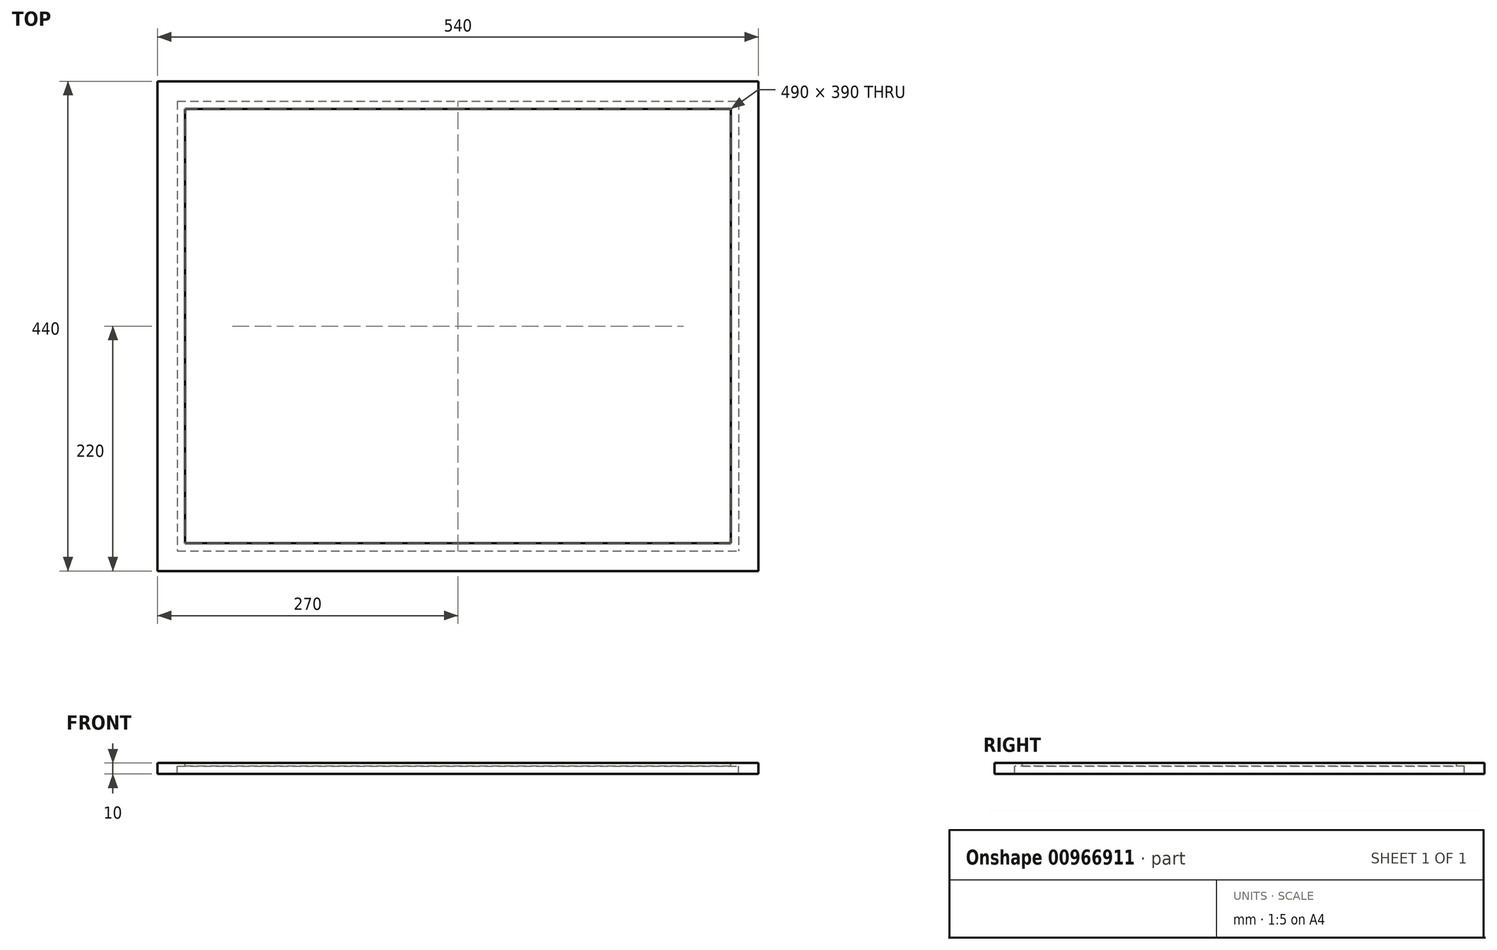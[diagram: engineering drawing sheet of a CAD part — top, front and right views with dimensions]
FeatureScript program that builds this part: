
annotation { "Feature Type Name" : "Feature", "Feature Type Description" : "" }
export const myFeature = defineFeature(function(context is Context, id is Id, definition is map)
    precondition{}
    {
        {
            var Q0;
            Q0=qCreatedBy(makeId("Top.planeOp"),FACE);
            var sketch = newSketch(context, id + "F0", { "sketchPlane" : qUnion([Q0])});
            skLineSegment(sketch, "E0.bottom", {"start": v(-270, 220) * mm, "end": v(270, 220) * mm});
            skLineSegment(sketch, "E0.top", {"start": v(-270, -220) * mm, "end": v(270, -220) * mm});
            skLineSegment(sketch, "E0.left", {"start": v(-270, 220) * mm, "end": v(-270, -220) * mm});
            skLineSegment(sketch, "E0.right", {"start": v(270, 220) * mm, "end": v(270, -220) * mm});
            skLineSegment(sketch, "E1.bottom", {"start": v(245, -195) * mm, "end": v(-245, -195) * mm});
            skLineSegment(sketch, "E1.top", {"start": v(245, 195) * mm, "end": v(-245, 195) * mm});
            skLineSegment(sketch, "E1.left", {"start": v(245, -195) * mm, "end": v(245, 195) * mm});
            skLineSegment(sketch, "E1.right", {"start": v(-245, -195) * mm, "end": v(-245, 195) * mm});
            skArc(sketch, "E2", {"start": v(270, 195) * mm, "mid": v(262.68, 212.68) * mm, "end": v(245, 220) * mm, "construction": true});
            skLineSegment(sketch, "E3.bottom", {"start": v(-252, 202) * mm, "end": v(252, 202) * mm});
            skLineSegment(sketch, "E3.top", {"start": v(-252, -202) * mm, "end": v(252, -202) * mm});
            skLineSegment(sketch, "E3.left", {"start": v(-252, 202) * mm, "end": v(-252, -202) * mm});
            skLineSegment(sketch, "E3.right", {"start": v(252, 202) * mm, "end": v(252, -202) * mm});
            skArc(sketch, "E4.trimOffspring", {"start": v(252, 195) * mm, "mid": v(249.95, 199.95) * mm, "end": v(245, 202) * mm, "construction": true});
            skSolve(sketch);
        }
        {
            var Q0;
            Q0=makeQuery(id+"F0.imprint","IMPRINT",FACE,{"disambiguationData":[TD([[makeQuery(id+"F0.imprint","IMPRINT",EDGE,{"derivedFrom":sQuery(id+"F0.wireOp",EDGE,"E0.bottom")}),-1.0]])]});
            var Q1;
            Q1=makeQuery(id+"F0.imprint","IMPRINT",FACE,{"disambiguationData":[TD([[makeQuery(id+"F0.imprint","IMPRINT",EDGE,{"derivedFrom":sQuery(id+"F0.wireOp",EDGE,"E1.bottom")}),1.0]])]});
            extrude(context, id + "F1", {"entities" : qUnion([Q0, Q1]), "oppositeDirection" : true, "depth" : 3 * mm, "offsetDistance" : 25 * mm});
        }
        {
            var Q0;
            Q0=makeQuery(id+"F0.imprint","IMPRINT",FACE,{"disambiguationData":[TD([[makeQuery(id+"F0.imprint","IMPRINT",EDGE,{"derivedFrom":sQuery(id+"F0.wireOp",EDGE,"E0.bottom")}),-1.0]])]});
            extrude(context, id + "F2", {"entities" : qUnion([Q0]), "operationType" : NewBodyOperationType.ADD, "oppositeDirection" : true, "depth" : 10 * mm, "offsetDistance" : 25 * mm});
        }
    });
